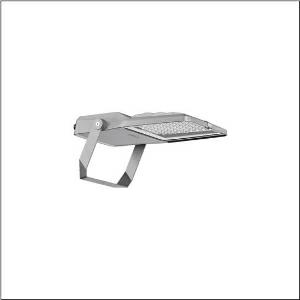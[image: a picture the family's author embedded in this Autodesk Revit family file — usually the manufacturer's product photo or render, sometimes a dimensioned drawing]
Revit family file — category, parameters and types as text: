
# Revit family: floodlight_fl_21_mini___pl64_5xa7775b2e1a_35e6
name_source: partatom
category: Lighting Fixtures
units: mm (PartAtom-declared; Revit-internal decimal feet)

## family parameters
Cut with Voids When Loaded = No
Host = Face
Light Source = No
Part Type = Normal
Room Calculation Point = No
Round Connector Dimension = Use Diameter
Shared = No

## types (1)
- --- (1 x LED, 6010 lm, 45.7 W, 3000K)
    Apparent Load = 46 VA
    CIE Flux Codes = 28 80 98 100 100
    Color Rendering = 70
    Color Temperature = 3000K
    Default Elevation = 1800 mm
    Description = Floodlight FL 21 mini, floodlight, primary light control with lens, of PMMA, primary optical cover: protective disc, of toughened safety glass, transparent, light distribution: PL64, light emission: direct distribution, installation type: surface-mounted, LED, High Power LED, rated luminous flux: 6.010lm, luminous efficacy: 132lm/W, light colour: 730, colour temperature: 3000K, control gear: Smart Interface (Zhaga), control: flexible luminous flux parameterisation, time-dependent luminous flux control, constant luminous flux control, overheat protection, pre-setting: logarithmic dimming characteristic, with terminal, 6-pole, mains connection: 220..240V, AC, 50/60Hz, start of lifetime: 46W, end of service life: 48W, reduction: 22W, luminaire housing, of diecast aluminium, powder-coated, Siteco® metallic grey (DB 702S), corrosivity category C5 mid according to DIN EN ISO 12944, suitable for swimming pools, chlorine-resistant, sealing non-destructively replaceable, mounting bracket, of steel, galvanised, powder-coated, Siteco® metallic grey (DB 702S), Smart Interface above, protection rating (complete): IP66, insulation class (complete): insulation class II (safety insulation), certification: CE, ENEC, VDE, protection symbol: D, impact resistance: IK08, permissible operating ambient temperature: -40..+40°C, permissible operating ambient temperature for outdoor applications: -40..+50°C, standard: DIN EN 12944, LABS conformity tested according to VDMA 24364:2018-05, packaging unit: 1 piece

Light Distribution: PL64
    Height = 70 mm
    Lamp = 1 x LED
    Lamp Light Flux = 6010 lm
    Lamp Power = 45.7 W
    Lamp count = 1
    Length = 485 mm
    Luminous efficacy = 132 lm/W
    Manufacturer = Siteco
    ModVariant = No
    Model = 5XA7775B2E1A
    Number of Poles = 1
    OnlyDefault = Yes
    Power Factor = 1
    Product Name = Floodlight FL 21 mini | PL64
    Product group = floodlight | pylon annexe
    ProductGroupID = 6200
    Protection Class = Protection class II
    Protection Degree = IP 66
    RLX_Detail_Level = 1
    RLX_Emergency_Light_Flux = 0 lm
    RLX_Emergency_Type = 0
    RLX_Emergency_Type_DB = No
    RlxData = <blob elided: 96085 chars, md5=f973dc3a>
    Socket = socket
    Standby Power = 0 W
    System Light Flux = 6010 lm
    System Power = 46 W
    Type Comments = factory setting: luminous flux: 100 % | dim-lin: 254 | 463 mA
    Type Image = l_1006845.jpg
    URL = http://relux.com
    VarID = @adj_165578
    Voltage = 0 V
    Weight = 0.00 kg
    Width = 337 mm

## geometry (parser evidence)
native form markers: Blend x4, Sweep x12
no freeform markers — native parametric forms only
